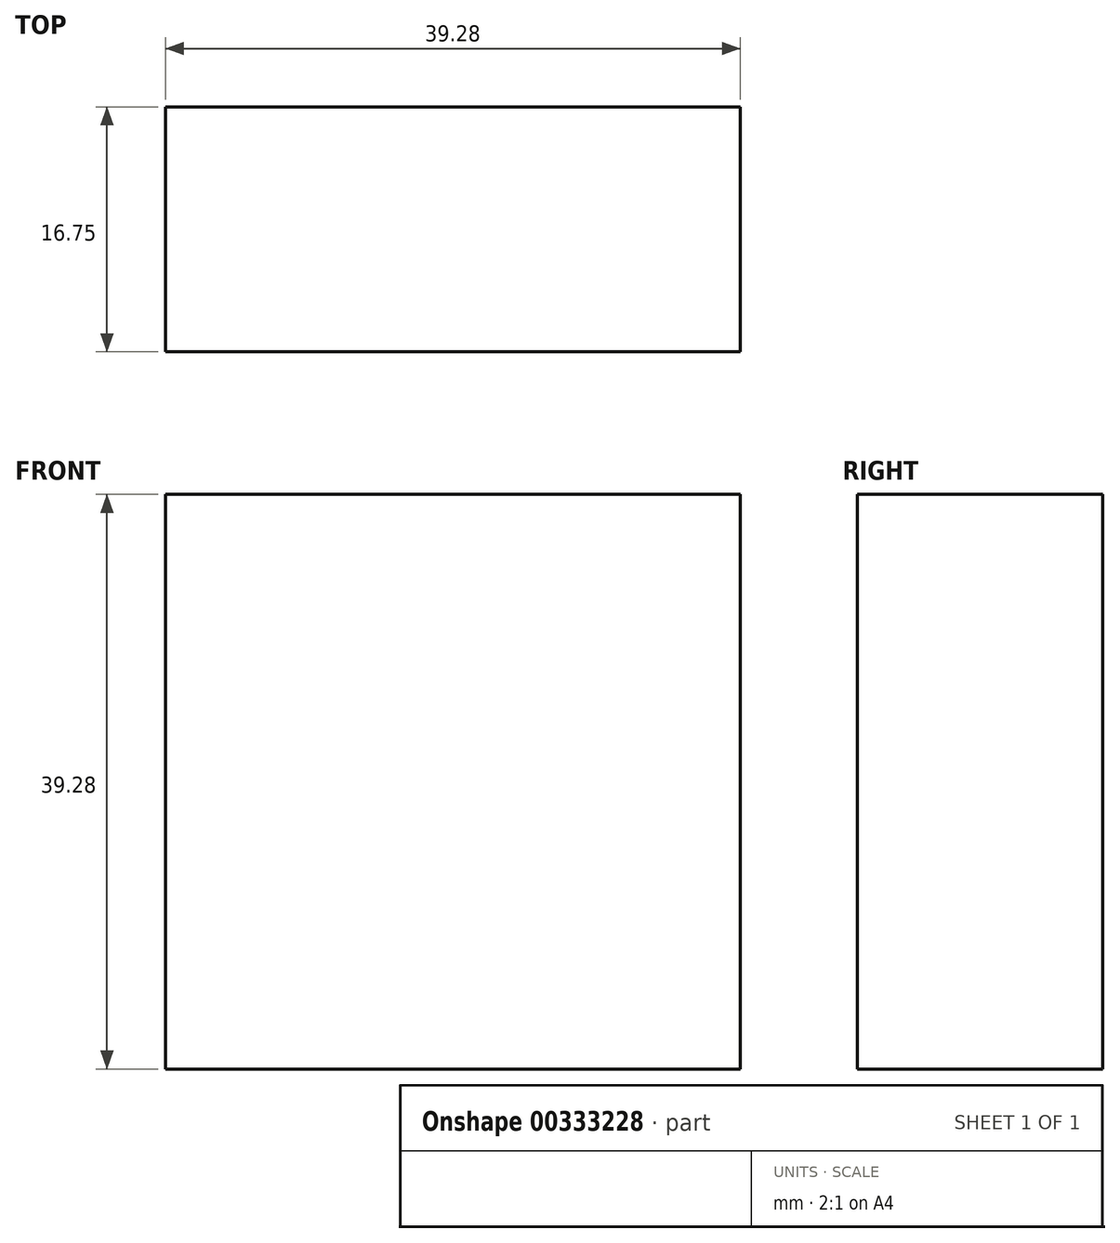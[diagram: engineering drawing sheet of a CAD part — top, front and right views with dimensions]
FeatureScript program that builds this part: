
annotation { "Feature Type Name" : "Feature", "Feature Type Description" : "" }
export const myFeature = defineFeature(function(context is Context, id is Id, definition is map)
    precondition{}
    {
        {
            var Q0;
            Q0=qCreatedBy(makeId("Front.planeOp"),FACE);
            var sketch = newSketch(context, id + "F0", { "sketchPlane" : qUnion([Q0])});
            skLineSegment(sketch, "E0.bottom", {"start": v(19.64, -19.64) * mm, "end": v(-19.64, -19.64) * mm});
            skLineSegment(sketch, "E0.top", {"start": v(19.64, 19.64) * mm, "end": v(-19.64, 19.64) * mm});
            skLineSegment(sketch, "E0.left", {"start": v(19.64, -19.64) * mm, "end": v(19.64, 19.64) * mm});
            skLineSegment(sketch, "E0.right", {"start": v(-19.64, -19.64) * mm, "end": v(-19.64, 19.64) * mm});
            skPoint(sketch, "E0.middle", {"position": v(0, 0) * mm});
            skSolve(sketch);
        }
        {
            var Q0;
            Q0=qSketchRegion(id+"F0",true);
            extrude(context, id + "F1", {"entities" : qUnion([Q0]), "depth" : 16.75 * mm});
        }
    });
